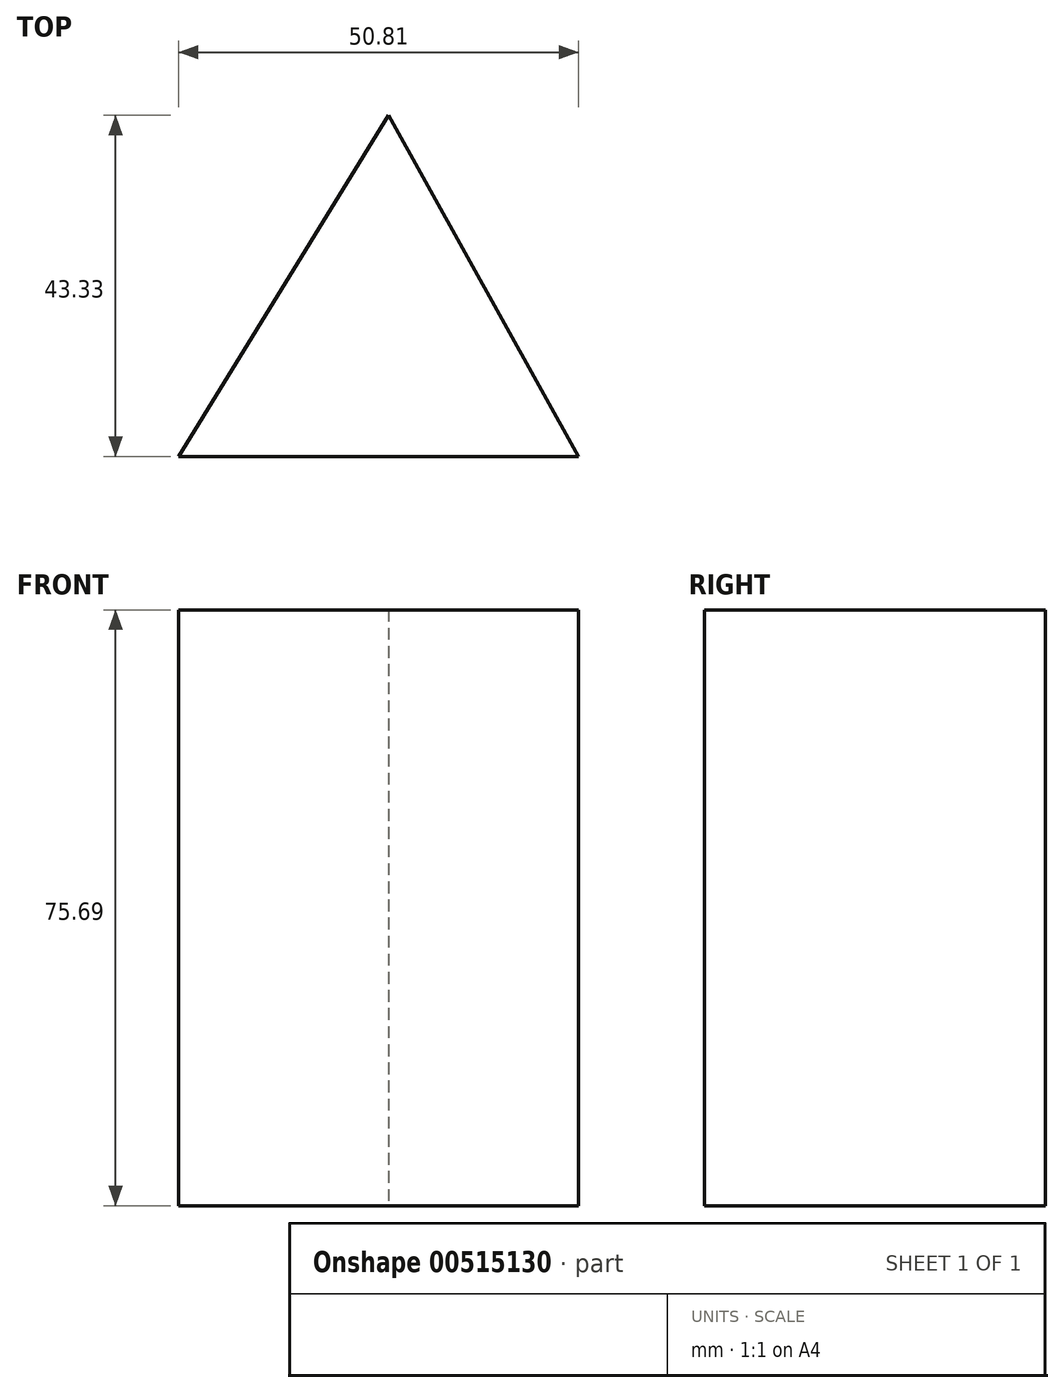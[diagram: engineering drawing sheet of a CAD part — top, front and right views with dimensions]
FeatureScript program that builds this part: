
annotation { "Feature Type Name" : "Feature", "Feature Type Description" : "" }
export const myFeature = defineFeature(function(context is Context, id is Id, definition is map)
    precondition{}
    {
        {
            var Q0;
            Q0=qCreatedBy(makeId("Top.planeOp"),FACE);
            var sketch = newSketch(context, id + "F0", { "sketchPlane" : qUnion([Q0])});
            skLineSegment(sketch, "E0", {"start": v(0, 28.95) * mm, "end": v(-26.66, -14.38) * mm});
            skLineSegment(sketch, "E1", {"start": v(-26.66, -14.38) * mm, "end": v(24.15, -14.38) * mm});
            skLineSegment(sketch, "E2", {"start": v(24.15, -14.38) * mm, "end": v(0, 28.95) * mm});
            skSolve(sketch);
        }
        {
            var Q0;
            Q0 = qSketchRegion(id + "F0", true);
            extrude(context, id + "F1", {"entities" : qUnion([Q0]), "depth" : 75.7 * mm, "offsetDistance" : 25.4 * mm});
        }
    });
